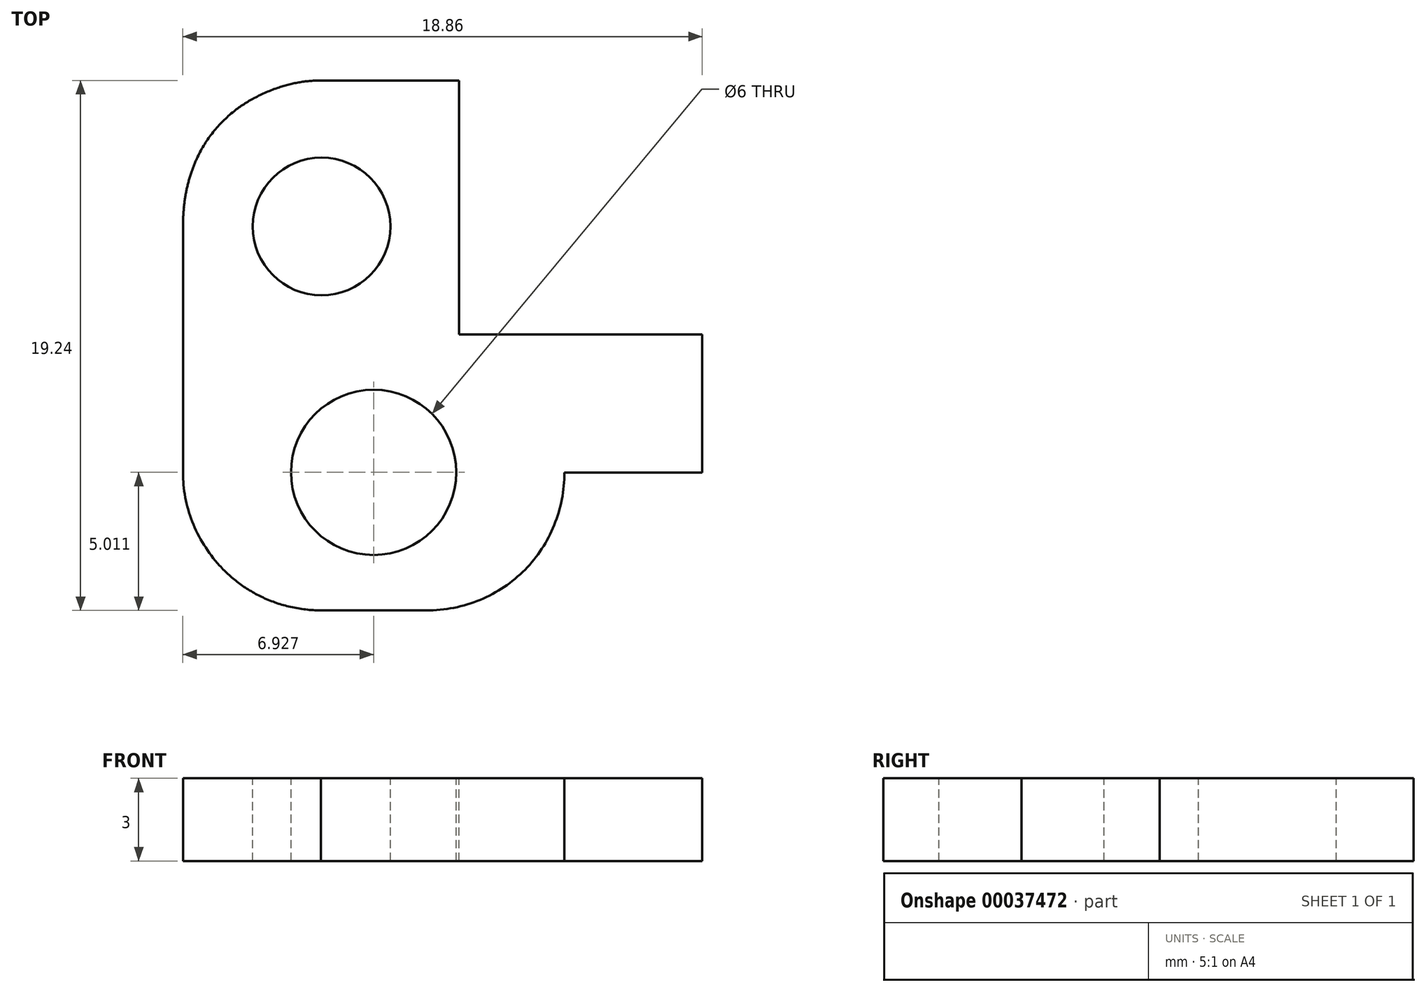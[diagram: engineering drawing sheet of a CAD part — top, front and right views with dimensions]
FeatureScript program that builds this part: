
annotation { "Feature Type Name" : "Feature", "Feature Type Description" : "" }
export const myFeature = defineFeature(function(context is Context, id is Id, definition is map)
    precondition{}
    {
        {
            var Q0;
            Q0=qCreatedBy(makeId("Top.planeOp"),FACE);
            var sketch = newSketch(context, id + "F0", { "sketchPlane" : qUnion([Q0])});
            skLineSegment(sketch, "E0", {"start": v(-1.72, -9.62) * mm, "end": v(-1.72, -9.62) * mm});
            skArc(sketch, "E1", {"start": v(-1.72, -9.62) * mm, "mid": v(-2.27, -9.59) * mm, "end": v(-2.82, -9.5) * mm});
            skArc(sketch, "E2", {"start": v(-2.82, -9.5) * mm, "mid": v(-3.33, -9.35) * mm, "end": v(-3.82, -9.16) * mm});
            skArc(sketch, "E3", {"start": v(-3.82, -9.16) * mm, "mid": v(-4.25, -8.93) * mm, "end": v(-4.66, -8.66) * mm});
            skArc(sketch, "E4", {"start": v(-4.66, -8.66) * mm, "mid": v(-5.05, -8.34) * mm, "end": v(-5.4, -8) * mm});
            skArc(sketch, "E5", {"start": v(-5.4, -8) * mm, "mid": v(-5.97, -7.24) * mm, "end": v(-6.39, -6.4) * mm});
            skArc(sketch, "E6", {"start": v(-6.39, -6.4) * mm, "mid": v(-6.64, -5.52) * mm, "end": v(-6.73, -4.6) * mm});
            skLineSegment(sketch, "E7", {"start": v(-6.73, -4.6) * mm, "end": v(-6.73, 4.32) * mm});
            skArc(sketch, "E8", {"start": v(-6.73, 4.32) * mm, "mid": v(-6.72, 4.68) * mm, "end": v(-6.69, 5.04) * mm});
            skArc(sketch, "E9", {"start": v(-6.69, 5.04) * mm, "mid": v(-6.65, 5.37) * mm, "end": v(-6.59, 5.69) * mm});
            skArc(sketch, "E10", {"start": v(-6.59, 5.69) * mm, "mid": v(-6.51, 6) * mm, "end": v(-6.42, 6.3) * mm});
            skArc(sketch, "E11", {"start": v(-6.42, 6.3) * mm, "mid": v(-6.32, 6.57) * mm, "end": v(-6.2, 6.84) * mm});
            skArc(sketch, "E12", {"start": v(-6.2, 6.84) * mm, "mid": v(-5.94, 7.31) * mm, "end": v(-5.63, 7.75) * mm});
            skArc(sketch, "E13", {"start": v(-5.63, 7.75) * mm, "mid": v(-5.27, 8.15) * mm, "end": v(-4.87, 8.5) * mm});
            skArc(sketch, "E14", {"start": v(-4.87, 8.5) * mm, "mid": v(-4.52, 8.76) * mm, "end": v(-4.14, 8.99) * mm});
            skArc(sketch, "E15", {"start": v(-4.14, 8.99) * mm, "mid": v(-3.7, 9.2) * mm, "end": v(-3.24, 9.37) * mm});
            skArc(sketch, "E16", {"start": v(-3.24, 9.37) * mm, "mid": v(-2.86, 9.48) * mm, "end": v(-2.47, 9.56) * mm});
            skArc(sketch, "E17", {"start": v(-2.47, 9.56) * mm, "mid": v(-2.1, 9.61) * mm, "end": v(-1.7, 9.62) * mm});
            skLineSegment(sketch, "E18", {"start": v(-1.7, 9.62) * mm, "end": v(3.3, 9.62) * mm});
            skLineSegment(sketch, "E19", {"start": v(3.3, 9.62) * mm, "end": v(3.3, 0.4) * mm});
            skLineSegment(sketch, "E20", {"start": v(3.3, 0.4) * mm, "end": v(7.13, 0.4) * mm});
            skLineSegment(sketch, "E21", {"start": v(7.13, 0.4) * mm, "end": v(7.13, -4.6) * mm});
            skArc(sketch, "E22", {"start": v(7.13, -4.6) * mm, "mid": v(7.03, -5.59) * mm, "end": v(6.75, -6.53) * mm});
            skArc(sketch, "E23", {"start": v(6.75, -6.53) * mm, "mid": v(6.3, -7.38) * mm, "end": v(5.7, -8.14) * mm});
            skArc(sketch, "E24", {"start": v(5.7, -8.14) * mm, "mid": v(4.94, -8.77) * mm, "end": v(4.07, -9.23) * mm});
            skArc(sketch, "E25", {"start": v(4.07, -9.23) * mm, "mid": v(3.1, -9.53) * mm, "end": v(2.1, -9.62) * mm});
            skLineSegment(sketch, "E26", {"start": v(2.1, -9.62) * mm, "end": v(-1.72, -9.62) * mm});
            skCircle(sketch, "E27", {"center": v(-1.7, 4.32) * mm, "radius": 2.5 * mm});
            skLineSegment(sketch, "E28", {"start": v(0.2, -9.62) * mm, "end": v(0.2, -2.14) * mm, "construction": true});
            skLineSegment(sketch, "E29", {"start": v(7.13, -4.6) * mm, "end": v(-6.73, -4.6) * mm, "construction": true});
            skCircle(sketch, "E30", {"center": v(0.2, -4.6) * mm, "radius": 3 * mm});
            skSolve(sketch);
        }
        {
            var Q0;
            Q0 = qSketchRegion(id + "F0", true);
            var Q1;
            Q1=makeQuery(id+"F0.imprint","IMPRINT",FACE,{"disambiguationData":[TD([[makeQuery(id+"F0.imprint","IMPRINT",EDGE,{"derivedFrom":sQuery(id+"F0.wireOp",EDGE,"E0")}),-1.0]])]});
            extrude(context, id + "F1", {"entities" : qUnion([Q0, Q1]), "oppositeDirection" : true, "depth" : 3 * mm});
        }
        {
            var Q0;
            Q0=makeQuery(id+"F1.opExtrude","SWEPT_FACE",FACE,{"disambiguationData":[OSD([sQuery(id+"F0.wireOp",EDGE,"E21")])]});
            extrude(context, id + "F2", {"entities" : qUnion([Q0]), "operationType" : NewBodyOperationType.ADD, "depth" : 5 * mm});
        }
    });
